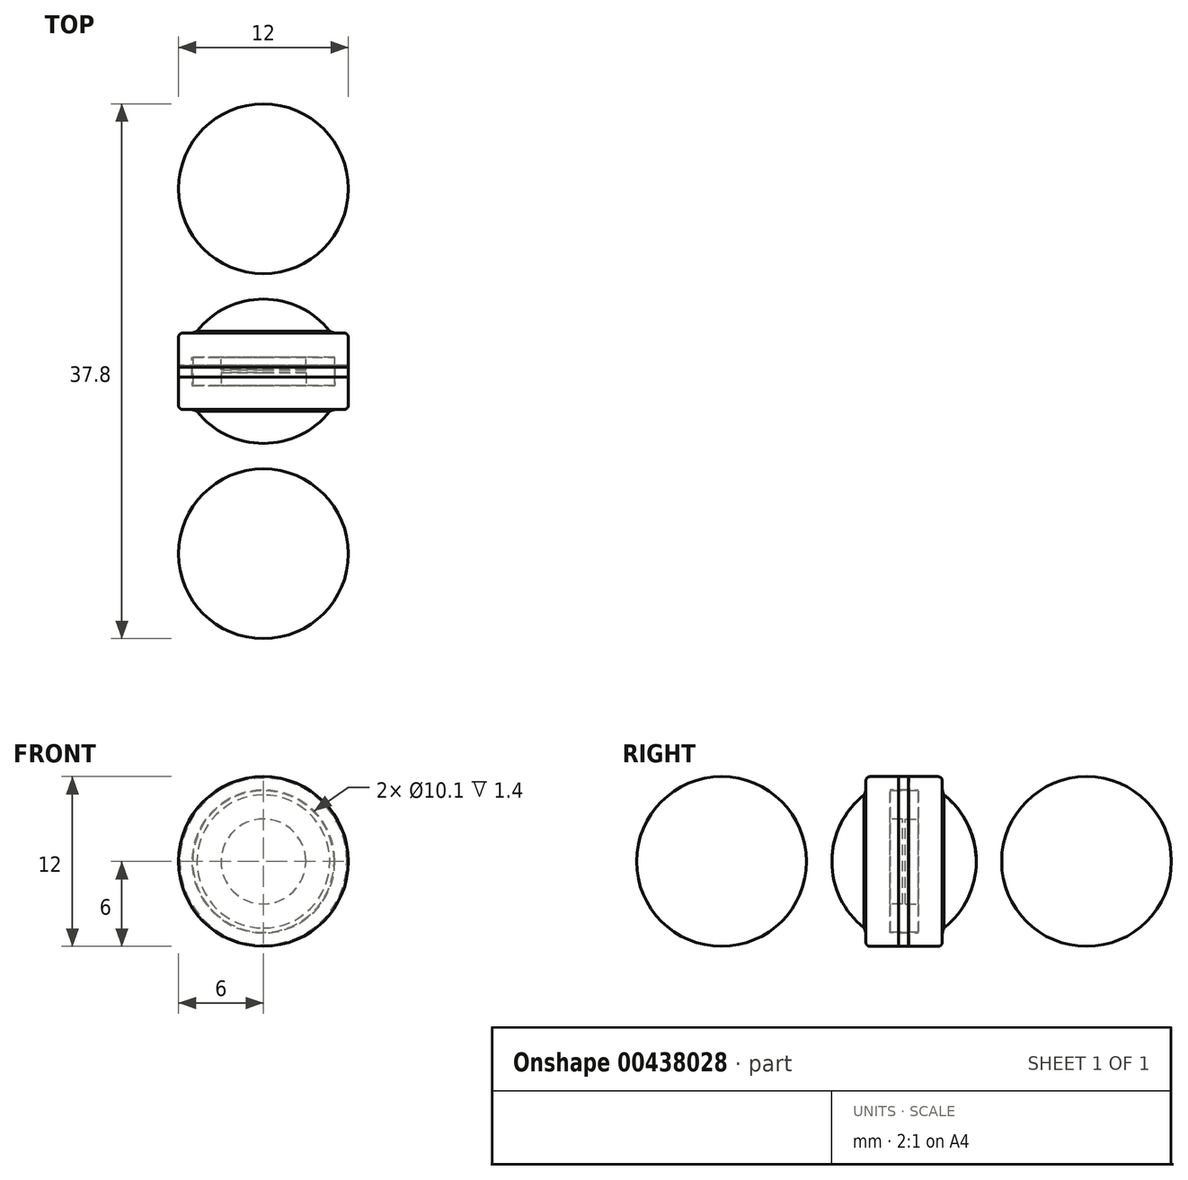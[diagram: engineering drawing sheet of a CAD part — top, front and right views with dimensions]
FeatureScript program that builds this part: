
annotation { "Feature Type Name" : "Feature", "Feature Type Description" : "" }
export const myFeature = defineFeature(function(context is Context, id is Id, definition is map)
    precondition{}
    {
        {
            var Q0;
            Q0=qCreatedBy(makeId("Right.planeOp"),FACE);
            var sketch = newSketch(context, id + "F0", { "sketchPlane" : qUnion([Q0])});
            skLineSegment(sketch, "E0", {"start": v(-1.4, 3) * mm, "end": v(-1.4, 5.05) * mm});
            skLineSegment(sketch, "E1", {"start": v(-1.4, 5.05) * mm, "end": v(0, 5.05) * mm});
            skLineSegment(sketch, "E2", {"start": v(0, 5.05) * mm, "end": v(0, 6) * mm});
            skLineSegment(sketch, "E3", {"start": v(0, 6) * mm, "end": v(-3.1, 6) * mm});
            skLineSegment(sketch, "E4", {"start": v(-3.1, 6) * mm, "end": v(-3.1, 5.2) * mm});
            skLineSegment(sketch, "E5", {"start": v(-5.5, 0) * mm, "end": v(-0.5, 0) * mm});
            skPoint(sketch, "E6.orphan", {"position": v(-3.1, 0) * mm});
            skArc(sketch, "E7", {"start": v(-3.23, 4.7) * mm, "mid": v(-4.9, 2.6) * mm, "end": v(-5.5, 0) * mm});
            skLineSegment(sketch, "E8", {"start": v(-0.5, 3) * mm, "end": v(-0.5, 0) * mm});
            skPoint(sketch, "E9.orphan", {"position": v(-1.4, 0) * mm});
            skLineSegment(sketch, "E10", {"start": v(-1.4, 3) * mm, "end": v(-0.5, 3) * mm});
            skPoint(sketch, "E11.orphan", {"position": v(-0.5, 2.52) * mm});
            skArc(sketch, "E12", {"start": v(-3.23, 4.7) * mm, "mid": v(-3.13, 4.94) * mm, "end": v(-3.1, 5.2) * mm});
            skPoint(sketch, "E13.orphan", {"position": v(-1.4, 2.52) * mm});
            skSolve(sketch);
        }
        {
            var Q0;
            Q0=qSketchRegion(id+"F0",true);
            var Q1;
            Q1=sQuery(id+"F0.wireOp",EDGE,"E5");
            revolve(context, id + "F1", {"entities" : qUnion([Q0]), "axis" : qUnion([Q1]), "revolveType" : RevolveType.FULL});
        }
        {
            var Q0;
            Q0=makeQuery(id+"F1.opRevolve","SWEPT_EDGE",EDGE,{"disambiguationData":[OSD([sQuery(id+"F0.wireOp",EDGE,"E3"),sQuery(id+"F0.wireOp",EDGE,"E4")])]});
            fillet(context, id + "F2", {"entities" : qUnion([Q0]), "radius" : 0.3 * mm, "tangentPropagation" : true, "allowEdgeOverflow" : false});
        }
        {
            var Q0;
            Q0=makeQuery(id+"F1.opRevolve","SWEPT_FACE",FACE,{"disambiguationData":[OSD([sQuery(id+"F0.wireOp",EDGE,"E0")])]});
            cPlane(context, id + "F3", {"entities" : qUnion([Q0]), "cplaneType" : CPlaneType.OFFSET, "offset" : 1 * mm, "width" : 150 * mm, "height" : 150 * mm});
        }
        {
            var Q0;
            Q0=makeQuery(id+"F1.opRevolve","SWEPT_BODY",BODY,{"disambiguationData":[OSD([sQuery(id+"F0.wireOp",EDGE,"E0"),sQuery(id+"F0.wireOp",EDGE,"E1"),sQuery(id+"F0.wireOp",EDGE,"E2"),sQuery(id+"F0.wireOp",EDGE,"E3"),sQuery(id+"F0.wireOp",EDGE,"E4"),sQuery(id+"F0.wireOp",EDGE,"E5"),sQuery(id+"F0.wireOp",EDGE,"E7"),sQuery(id+"F0.wireOp",EDGE,"2RYD5lRM-PL3K-YWC5-MBGl-w0IWwY0Oq9dN"),sQuery(id+"F0.wireOp",EDGE,"59uXxaTu-KyhA-3nZE-CTbu-j2CFj0NGySWv")])]});
            var Q1;
            Q1=qCreatedBy(id+"F3.planeOp",FACE);
            mirror(context, id + "F4", {"entities" : qUnion([Q0]), "mirrorPlane" : qUnion([Q1])});
        }
        {
            var Q0;
            Q0=qCreatedBy(makeId("Right.planeOp"),FACE);
            var sketch = newSketch(context, id + "F5", { "sketchPlane" : qUnion([Q0])});
            skArc(sketch, "E14", {"start": v(18.5, 0) * mm, "mid": v(12.5, 6) * mm, "end": v(6.5, 0) * mm});
            skLineSegment(sketch, "E15", {"start": v(18.5, 0) * mm, "end": v(6.5, 0) * mm});
            skSolve(sketch);
        }
        {
            var Q0;
            Q0=qSketchRegion(id+"F5",true);
            var Q1;
            Q1=sQuery(id+"F5.wireOp",EDGE,"E15");
            revolve(context, id + "F6", {"entities" : qUnion([Q0]), "axis" : qUnion([Q1]), "revolveType" : RevolveType.FULL});
        }
        {
            var Q0;
            Q0=makeQuery(id+"FeZ0k1wJocLlwxZ_4.boolean.opBoolean","SPLIT",EDGE,{"disambiguationData":[OD(0.0)],"derivedFrom":makeQuery(id+"F1.opRevolve","SWEPT_EDGE",EDGE,{"disambiguationData":[OSD([sQuery(id+"F0.wireOp",EDGE,"E2"),sQuery(id+"F0.wireOp",EDGE,"E3")])]})});
            var Q1;
            Q1=makeQuery(id+"FeZ0k1wJocLlwxZ_4.boolean.opBoolean","SPLIT",EDGE,{"disambiguationData":[OD(1.0)],"derivedFrom":makeQuery(id+"F1.opRevolve","SWEPT_EDGE",EDGE,{"disambiguationData":[OSD([sQuery(id+"F0.wireOp",EDGE,"E2"),sQuery(id+"F0.wireOp",EDGE,"E3")])]})});
            chamfer(context, id + "F7", {"entities" : qUnion([Q0, Q1]), "width" : .1 * mm, "tangentPropagation" : true});
        }
        {
            var Q0;
            Q0=makeQuery(id+"F6.opRevolve","SWEPT_BODY",BODY,{"disambiguationData":[OSD([sQuery(id+"F5.wireOp",EDGE,"E14"),sQuery(id+"F5.wireOp",EDGE,"E15")])]});
            var Q1;
            Q1=qCreatedBy(id+"F3.planeOp",FACE);
            mirror(context, id + "F8", {"entities" : qUnion([Q0]), "mirrorPlane" : qUnion([Q1])});
        }
        {
            var Q0;
            Q0=makeQuery(id+"F1.opRevolve","SWEPT_FACE",FACE,{"disambiguationData":[OSD([sQuery(id+"F0.wireOp",EDGE,"E0")])]});
            var sketch = newSketch(context, id + "F9", { "sketchPlane" : qUnion([Q0])});
            skCircle(sketch, "E16", {"center": v(0, 0) * mm, "radius": 5 * mm});
            skSolve(sketch);
        }
        {
            var Q0;
            Q0=qSketchRegion(id+"F9",true);
            extrude(context, id + "F10", {"entities" : qUnion([Q0]), "depth" : 2 * mm});
        }
    });
